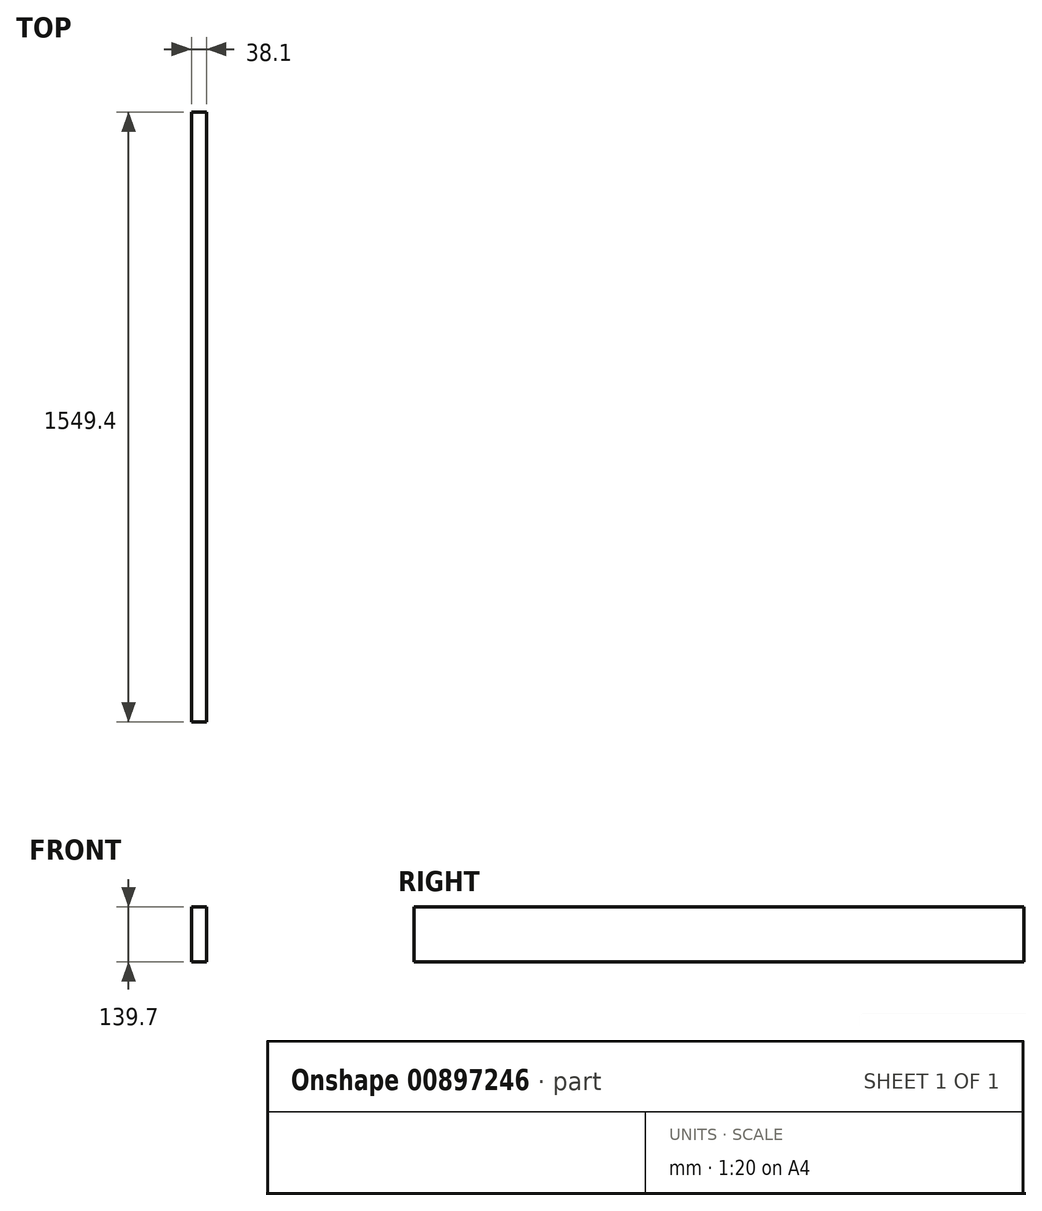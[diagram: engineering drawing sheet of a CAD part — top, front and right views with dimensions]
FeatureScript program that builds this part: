
annotation { "Feature Type Name" : "Feature", "Feature Type Description" : "" }
export const myFeature = defineFeature(function(context is Context, id is Id, definition is map)
    precondition{}
    {
        {
            var Q0;
            Q0=qCreatedBy(makeId("Front.planeOp"),FACE);
            var sketch = newSketch(context, id + "F0", { "sketchPlane" : qUnion([Q0])});
            skLineSegment(sketch, "E0.bottom", {"start": v(-19.05, 69.85) * mm, "end": v(19.05, 69.85) * mm});
            skLineSegment(sketch, "E0.top", {"start": v(-19.05, -69.85) * mm, "end": v(19.05, -69.85) * mm});
            skLineSegment(sketch, "E0.left", {"start": v(-19.05, 69.85) * mm, "end": v(-19.05, -69.85) * mm});
            skLineSegment(sketch, "E0.right", {"start": v(19.05, 69.85) * mm, "end": v(19.05, -69.85) * mm});
            skPoint(sketch, "E0.middle", {"position": v(0, 0) * mm});
            skSolve(sketch);
        }
        {
            var Q0;
            Q0=makeQuery(id+"F0.imprint","IMPRINT",FACE,{"disambiguationData":[TD([[makeQuery(id+"F0.imprint","IMPRINT",EDGE,{"derivedFrom":sQuery(id+"F0.wireOp",EDGE,"E0.bottom")}),-1.0]])]});
            extrude(context, id + "F1", {"entities" : qUnion([Q0]), "depth" : 1549.4 * mm, "offsetDistance" : 25.4 * mm});
        }
    });
